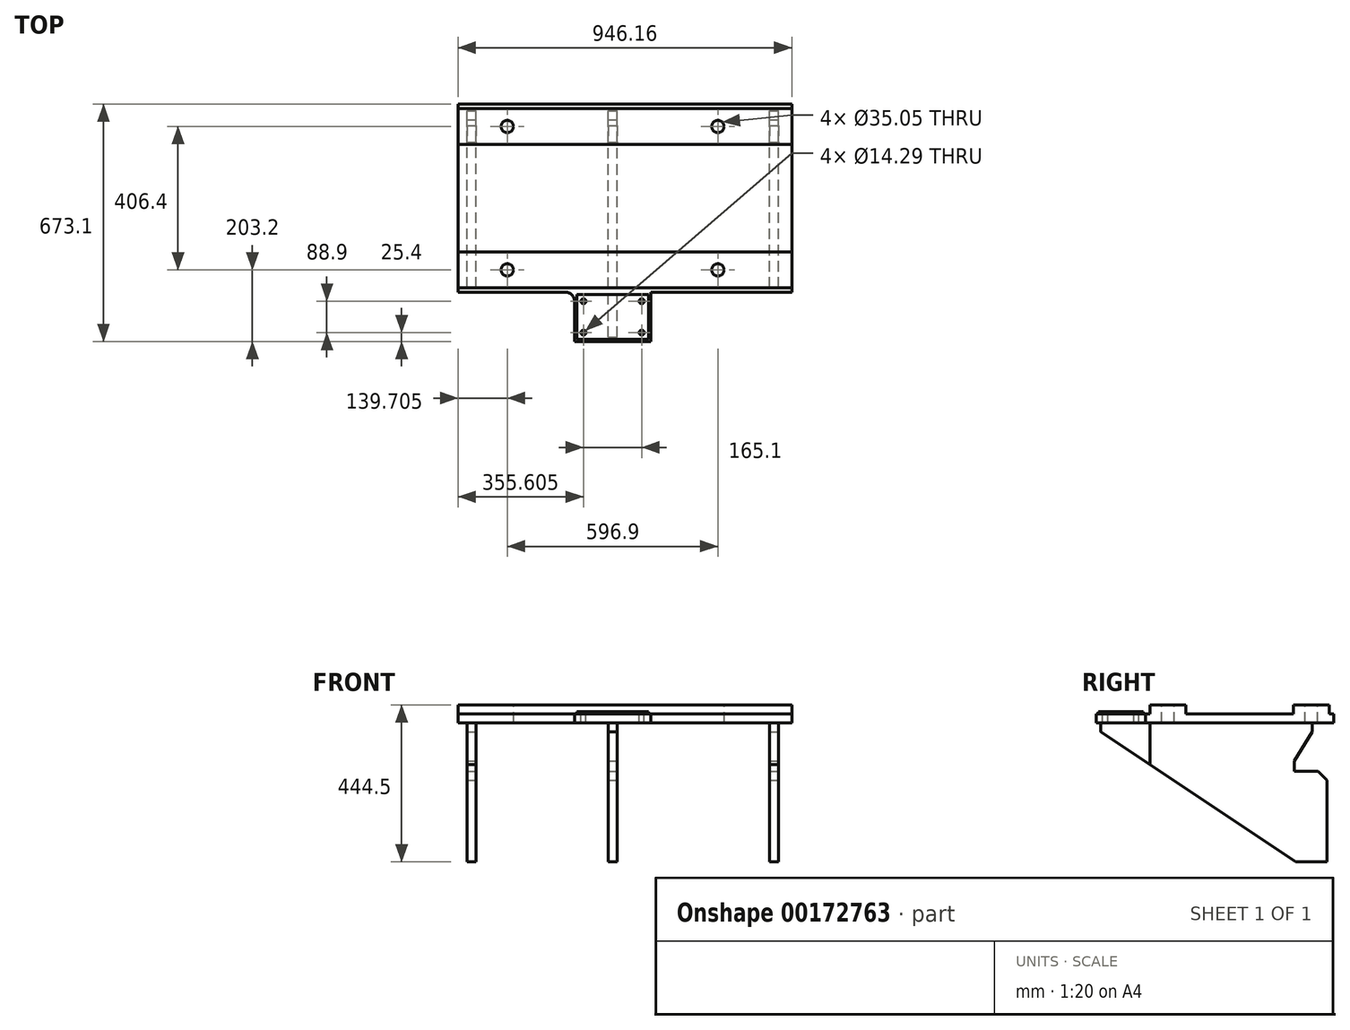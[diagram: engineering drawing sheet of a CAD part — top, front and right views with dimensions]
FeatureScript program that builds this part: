
annotation { "Feature Type Name" : "Feature", "Feature Type Description" : "" }
export const myFeature = defineFeature(function(context is Context, id is Id, definition is map)
    precondition{}
    {
        {
            var Q0;
            Q0=qCreatedBy(makeId("Top.planeOp"),FACE);
            var sketch = newSketch(context, id + "F0", { "sketchPlane" : qUnion([Q0])});
            skLineSegment(sketch, "E0.rect.bottom", {"start": v(-473.07, 266.7) * mm, "end": v(473.08, 266.7) * mm});
            skLineSegment(sketch, "E0.rect.top", {"start": v(-473.08, -266.7) * mm, "end": v(473.07, -266.7) * mm});
            skLineSegment(sketch, "E0.rect.left", {"start": v(-473.08, 266.7) * mm, "end": v(-473.08, -266.7) * mm});
            skLineSegment(sketch, "E0.rect.right", {"start": v(473.08, 266.7) * mm, "end": v(473.07, -266.7) * mm});
            skPoint(sketch, "E0.rect.middle", {"position": v(0, 0) * mm});
            skSolve(sketch);
        }
        {
            var Q0;
            Q0=qSketchRegion(id+"F0",true);
            extrude(context, id + "F1", {"entities" : qUnion([Q0]), "oppositeDirection" : true, "depth" : 25.4 * mm});
        }
        {
            var Q0;
            Q0=makeQuery(id+"F1.opExtrude","CAP_FACE",FACE,{"disambiguationData":[OSD([sQuery(id+"F0.wireOp",EDGE,"E0.rect.bottom"),sQuery(id+"F0.wireOp",EDGE,"E0.rect.top"),sQuery(id+"F0.wireOp",EDGE,"E0.rect.left"),sQuery(id+"F0.wireOp",EDGE,"E0.rect.right")])],"isStart":true});
            var sketch = newSketch(context, id + "F2", { "sketchPlane" : qUnion([Q0])});
            skLineSegment(sketch, "E1.0", {"start": v(-333.38, 266.7) * mm, "end": v(-333.38, -266.7) * mm, "construction": true});
            skLineSegment(sketch, "E2.0", {"start": v(-34.92, 266.7) * mm, "end": v(-34.93, -266.7) * mm, "construction": true});
            skLineSegment(sketch, "E3.0", {"start": v(-473.08, -266.7) * mm, "end": v(473.07, -266.7) * mm});
            skLineSegment(sketch, "E4.0", {"start": v(-473.08, -406.4) * mm, "end": v(473.07, -406.4) * mm});
            skLineSegment(sketch, "E5.0", {"start": v(-142.87, 266.7) * mm, "end": v(-142.88, -266.7) * mm, "construction": true});
            skLineSegment(sketch, "E6.bottom", {"start": v(-142.88, -266.7) * mm, "end": v(73.02, -266.7) * mm});
            skLineSegment(sketch, "E6.top", {"start": v(-142.88, -406.4) * mm, "end": v(73.02, -406.4) * mm});
            skLineSegment(sketch, "E6.left", {"start": v(-142.88, -266.7) * mm, "end": v(-142.88, -406.4) * mm});
            skLineSegment(sketch, "E6.right", {"start": v(73.02, -266.7) * mm, "end": v(73.02, -406.4) * mm});
            skSolve(sketch);
        }
        {
            var Q0;
            Q0=qSketchRegion(id+"F2",true);
            extrude(context, id + "F3", {"entities" : qUnion([Q0]), "operationType" : NewBodyOperationType.ADD, "oppositeDirection" : true, "depth" : 25.4 * mm});
        }
        {
            var Q0;
            Q0=makeQuery(id+"F3.opExtrude","SWEPT_EDGE",EDGE,{"disambiguationData":[OSD([sQuery(id+"F2.wireOp",EDGE,"E3.0"),sQuery(id+"F2.wireOp",EDGE,"E6.bottom"),sQuery(id+"F2.wireOp",EDGE,"E6.left")])]});
            var Q1;
            Q1=makeQuery(id+"F3.opExtrude","SWEPT_EDGE",EDGE,{"disambiguationData":[OSD([sQuery(id+"F2.wireOp",EDGE,"E3.0"),sQuery(id+"F2.wireOp",EDGE,"E6.bottom"),sQuery(id+"F2.wireOp",EDGE,"E6.right")])]});
            fillet(context, id + "F4", {"entities" : qUnion([Q0, Q1]), "radius" : 25.4 * mm, "tangentPropagation" : true, "allowEdgeOverflow" : false});
        }
        {
            var Q0;
            Q0=makeQuery(id+"F3.boolean.opBoolean","MERGE",FACE,{"derivedFrom":[makeQuery(id+"F1.opExtrude","CAP_FACE",FACE,{"disambiguationData":[OSD([sQuery(id+"F0.wireOp",EDGE,"E0.rect.bottom"),sQuery(id+"F0.wireOp",EDGE,"E0.rect.top"),sQuery(id+"F0.wireOp",EDGE,"E0.rect.left"),sQuery(id+"F0.wireOp",EDGE,"E0.rect.right")])],"isStart":true}),makeQuery(id+"F3.opExtrude","CAP_FACE",FACE,{"disambiguationData":[OSD([sQuery(id+"F2.wireOp",EDGE,"E6.bottom"),sQuery(id+"F2.wireOp",EDGE,"E6.top"),sQuery(id+"F2.wireOp",EDGE,"E6.left"),sQuery(id+"F2.wireOp",EDGE,"E6.right")])],"isStart":true})]});
            var sketch = newSketch(context, id + "F5", { "sketchPlane" : qUnion([Q0])});
            skLineSegment(sketch, "E7.0", {"start": v(-473.08, 254) * mm, "end": v(473.08, 254) * mm});
            skLineSegment(sketch, "E8.0", {"start": v(-473.08, 152.4) * mm, "end": v(473.08, 152.4) * mm});
            skLineSegment(sketch, "E9.0", {"start": v(-473.08, -152.4) * mm, "end": v(473.08, -152.4) * mm});
            skLineSegment(sketch, "E10.0", {"start": v(-473.08, -254) * mm, "end": v(473.08, -254) * mm});
            skLineSegment(sketch, "E11.0", {"start": v(473.08, 266.7) * mm, "end": v(473.07, -266.7) * mm});
            skLineSegment(sketch, "E12.0", {"start": v(-473.08, 266.7) * mm, "end": v(-473.08, -266.7) * mm});
            skSolve(sketch);
        }
        {
            var Q0;
            {var subQ2=sQuery(id+"F5.wireOp",EDGE,"E7.0");Q0=makeQuery(id+"F5.imprint","IMPRINT",FACE,{"disambiguationData":[TD([[makeQuery(id+"F5.imprint","IMPRINT",EDGE,{"derivedFrom":subQ2}),-1.0]])]});}
            var Q1;
            {var subQ2=sQuery(id+"F5.wireOp",EDGE,"E9.0");Q1=makeQuery(id+"F5.imprint","IMPRINT",FACE,{"disambiguationData":[TD([[makeQuery(id+"F5.imprint","IMPRINT",EDGE,{"derivedFrom":subQ2}),-1.0]])]});}
            extrude(context, id + "F6", {"entities" : qUnion([Q0, Q1]), "operationType" : NewBodyOperationType.ADD, "depth" : 25.4 * mm});
        }
        {
            var Q0;
            Q0=makeQuery(id+"F6.opExtrude","CAP_FACE",FACE,{"disambiguationData":[OSD([sQuery(id+"F5.wireOp",EDGE,"E7.0"),sQuery(id+"F5.wireOp",EDGE,"E8.0"),sQuery(id+"F5.wireOp",EDGE,"E11.0"),sQuery(id+"F5.wireOp",EDGE,"E12.0")])],"isStart":false});
            var sketch = newSketch(context, id + "F7", { "sketchPlane" : qUnion([Q0])});
            skLineSegment(sketch, "E13.0", {"start": v(-473.08, 266.7) * mm, "end": v(473.08, 266.7) * mm, "construction": true});
            skLineSegment(sketch, "E14.0", {"start": v(-473.08, 0) * mm, "end": v(473.08, 0) * mm, "construction": true});
            skLineSegment(sketch, "E15.0", {"start": v(-142.88, -406.4) * mm, "end": v(73.02, -406.4) * mm, "construction": true});
            skLineSegment(sketch, "E16", {"start": v(-34.93, -406.4) * mm, "end": v(-34.93, 332.02) * mm, "construction": true});
            skLineSegment(sketch, "E17.0", {"start": v(-473.08, 203.2) * mm, "end": v(473.08, 203.2) * mm, "construction": true});
            skLineSegment(sketch, "E18.0", {"start": v(-473.08, -203.2) * mm, "end": v(473.08, -203.2) * mm, "construction": true});
            skLineSegment(sketch, "E19.0", {"start": v(-333.38, -406.4) * mm, "end": v(-333.38, 332.02) * mm, "construction": true});
            skCircle(sketch, "E20", {"center": v(-333.38, 203.2) * mm, "radius": 17.53 * mm});
            skCircle(sketch, "E21", {"center": v(-333.38, -203.2) * mm, "radius": 17.53 * mm});
            skCircle(sketch, "E22.MirrorC", {"center": v(263.53, -203.2) * mm, "radius": 17.53 * mm});
            skCircle(sketch, "E23.MirrorC", {"center": v(263.53, 203.2) * mm, "radius": 17.53 * mm});
            skSolve(sketch);
        }
        {
            var Q0;
            Q0=qSketchRegion(id+"F7",true);
            extrude(context, id + "F8", {"entities" : qUnion([Q0]), "operationType" : NewBodyOperationType.REMOVE, "endBound" : BoundingType.THROUGH_ALL, "oppositeDirection" : true, "depth" : 25.4 * mm});
        }
        {
            var Q0;
            {var subQ0=sQuery(id+"F0.wireOp",EDGE,"E0.rect.top");var subQ1=sQuery(id+"F0.wireOp",EDGE,"E0.rect.left");var subQ2=sQuery(id+"F0.wireOp",EDGE,"E0.rect.right");var subQ3=sQuery(id+"F2.wireOp",EDGE,"E6.bottom");var subQ4=sQuery(id+"F2.wireOp",EDGE,"E6.top");var subQ5=sQuery(id+"F2.wireOp",EDGE,"E6.left");var subQ6=sQuery(id+"F2.wireOp",EDGE,"E6.right");Q0=makeQuery(id+"F6.boolean.opBoolean","SPLIT",FACE,{"disambiguationData":[TD([makeQuery(id+"F1.opExtrude","SWEPT_FACE",FACE,{"disambiguationData":[OSD([subQ0])]})])],"derivedFrom":makeQuery(id+"F3.boolean.opBoolean","MERGE",FACE,{"derivedFrom":[makeQuery(id+"F1.opExtrude","CAP_FACE",FACE,{"disambiguationData":[OSD([sQuery(id+"F0.wireOp",EDGE,"E0.rect.bottom"),subQ0,subQ1,subQ2])],"isStart":true}),makeQuery(id+"F3.opExtrude","CAP_FACE",FACE,{"disambiguationData":[OSD([subQ3,subQ4,subQ5,subQ6])],"isStart":true})]})});}
            var sketch = newSketch(context, id + "F9", { "sketchPlane" : qUnion([Q0])});
            skLineSegment(sketch, "E24", {"start": v(-34.93, -406.4) * mm, "end": v(-34.93, -216.21) * mm, "construction": true});
            skLineSegment(sketch, "E25.0", {"start": v(-142.88, -400.05) * mm, "end": v(73.02, -400.05) * mm});
            skLineSegment(sketch, "E26.0", {"start": v(-142.88, -273.05) * mm, "end": v(73.02, -273.05) * mm});
            skLineSegment(sketch, "E27.0", {"start": v(-136.53, -406.4) * mm, "end": v(-136.53, -216.21) * mm});
            skLineSegment(sketch, "E28.0", {"start": v(66.67, -406.4) * mm, "end": v(66.67, -216.21) * mm});
            skSolve(sketch);
        }
        {
            var Q0;
            Q0=qSketchRegion(id+"F9",true);
            extrude(context, id + "F10", {"entities" : qUnion([Q0]), "operationType" : NewBodyOperationType.ADD, "depth" : 6.35 * mm});
        }
        {
            var Q0;
            Q0=makeQuery(id+"F10.opExtrude","CAP_FACE",FACE,{"disambiguationData":[OSD([sQuery(id+"F9.wireOp",EDGE,"E25.0"),sQuery(id+"F9.wireOp",EDGE,"E26.0"),sQuery(id+"F9.wireOp",EDGE,"E27.0"),sQuery(id+"F9.wireOp",EDGE,"E28.0")])],"isStart":false});
            var sketch = newSketch(context, id + "F11", { "sketchPlane" : qUnion([Q0])});
            skLineSegment(sketch, "E29", {"start": v(-34.93, -400.05) * mm, "end": v(-34.93, -273.05) * mm, "construction": true});
            skLineSegment(sketch, "E30.0", {"start": v(-473.08, 152.4) * mm, "end": v(473.08, 152.4) * mm, "construction": true});
            skLineSegment(sketch, "E31.0", {"start": v(-473.08, -152.4) * mm, "end": v(473.08, -152.4) * mm, "construction": true});
            skLineSegment(sketch, "E32", {"start": v(0, 152.4) * mm, "end": v(0, -152.4) * mm, "construction": true});
            skLineSegment(sketch, "E33", {"start": v(0, 0) * mm, "end": v(-542.05, 0) * mm, "construction": true});
            skLineSegment(sketch, "E34.0", {"start": v(0, -203.2) * mm, "end": v(-542.05, -203.2) * mm, "construction": true});
            skLineSegment(sketch, "E35.0", {"start": v(0, -292.1) * mm, "end": v(-542.05, -292.1) * mm, "construction": true});
            skLineSegment(sketch, "E36.0", {"start": v(0, -381) * mm, "end": v(-542.05, -381) * mm, "construction": true});
            skLineSegment(sketch, "E37.0", {"start": v(-117.48, -400.05) * mm, "end": v(-117.48, -273.05) * mm, "construction": true});
            skPoint(sketch, "E38", {"position": v(-117.48, -292.1) * mm});
            skPoint(sketch, "E39", {"position": v(-117.48, -381) * mm});
            skPoint(sketch, "E40.MirrorP", {"position": v(47.62, -381) * mm});
            skPoint(sketch, "E41.MirrorP", {"position": v(47.62, -292.1) * mm});
            skSolve(sketch);
        }
        {
            var Q0;
            Q0=sQuery(id+"F11.wireOp",VERTEX,"E38");
            var Q1;
            Q1=sQuery(id+"F11.wireOp",VERTEX,"E39");
            var Q2;
            Q2=sQuery(id+"F11.wireOp",VERTEX,"E41.MirrorP");
            var Q3;
            Q3=sQuery(id+"F11.wireOp",VERTEX,"E40.MirrorP");
            var Q4;
            Q4=makeQuery(id+"F1.opExtrude","SWEPT_BODY",BODY,{"disambiguationData":[OSD([sQuery(id+"F0.wireOp",EDGE,"E0.rect.bottom"),sQuery(id+"F0.wireOp",EDGE,"E0.rect.top"),sQuery(id+"F0.wireOp",EDGE,"E0.rect.left"),sQuery(id+"F0.wireOp",EDGE,"E0.rect.right")])]});
            hole(context, id + "F12", {"style" : HoleStyle.SIMPLE, "holeDiameter" : 14.29 * mm, "endStyle" : HoleEndStyle.THROUGH, "locations" : qUnion([Q0, Q1, Q2, Q3]), "scope" : qUnion([Q4])});
        }
        {
            var Q0;
            Q0=makeQuery(id+"F3.boolean.opBoolean","MERGE",FACE,{"derivedFrom":[makeQuery(id+"F1.opExtrude","CAP_FACE",FACE,{"disambiguationData":[OSD([sQuery(id+"F0.wireOp",EDGE,"E0.rect.bottom"),sQuery(id+"F0.wireOp",EDGE,"E0.rect.top"),sQuery(id+"F0.wireOp",EDGE,"E0.rect.left"),sQuery(id+"F0.wireOp",EDGE,"E0.rect.right")])],"isStart":false}),makeQuery(id+"F3.opExtrude","CAP_FACE",FACE,{"disambiguationData":[OSD([sQuery(id+"F2.wireOp",EDGE,"E6.bottom"),sQuery(id+"F2.wireOp",EDGE,"E6.top"),sQuery(id+"F2.wireOp",EDGE,"E6.left"),sQuery(id+"F2.wireOp",EDGE,"E6.right")])],"isStart":false})]});
            var sketch = newSketch(context, id + "F13", { "sketchPlane" : qUnion([Q0])});
            skLineSegment(sketch, "E42.0", {"start": v(-473.08, -247.65) * mm, "end": v(473.08, -247.65) * mm});
            skLineSegment(sketch, "E43", {"start": v(-34.93, 406.4) * mm, "end": v(-34.93, -266.7) * mm, "construction": true});
            skLineSegment(sketch, "E44.0", {"start": v(-473.08, 393.45) * mm, "end": v(473.08, 393.45) * mm});
            skLineSegment(sketch, "E45.0", {"start": v(-473.08, 254) * mm, "end": v(-422.28, 254) * mm});
            skLineSegment(sketch, "E46.0", {"start": v(-47.63, 393.45) * mm, "end": v(-47.63, -247.65) * mm});
            skLineSegment(sketch, "E47.0", {"start": v(-22.23, 393.45) * mm, "end": v(-22.23, -247.65) * mm});
            skLineSegment(sketch, "E48.0", {"start": v(-447.68, 406.4) * mm, "end": v(-447.68, 393.45) * mm});
            skLineSegment(sketch, "E49.0", {"start": v(-422.28, 406.4) * mm, "end": v(-422.28, 393.45) * mm});
            skLineSegment(sketch, "E50.0", {"start": v(434.98, 406.4) * mm, "end": v(434.98, 393.45) * mm});
            skLineSegment(sketch, "E51.0", {"start": v(409.58, 406.4) * mm, "end": v(409.58, 393.45) * mm});
            skLineSegment(sketch, "E52.trimOffspring", {"start": v(-447.68, 254) * mm, "end": v(-447.68, -247.65) * mm});
            skLineSegment(sketch, "E53.trimOffspring", {"start": v(-422.28, 254) * mm, "end": v(-422.28, -247.65) * mm});
            skLineSegment(sketch, "E54.trimOffspring", {"start": v(409.58, 254) * mm, "end": v(409.58, -247.65) * mm});
            skLineSegment(sketch, "E55.trimOffspring", {"start": v(434.98, 254) * mm, "end": v(434.98, -247.65) * mm});
            skLineSegment(sketch, "E56.trimOffspring", {"start": v(409.58, 254) * mm, "end": v(473.08, 254) * mm});
            skLineSegment(sketch, "E57.trimOffspring", {"start": v(-47.63, 254) * mm, "end": v(-22.23, 254) * mm, "construction": true});
            skSolve(sketch);
        }
        {
            var Q0;
            {var subQ2=sQuery(id+"F13.wireOp",EDGE,"E54.trimOffspring");Q0=makeQuery(id+"F13.imprint","IMPRINT",FACE,{"disambiguationData":[TD([[makeQuery(id+"F13.imprint","IMPRINT",EDGE,{"derivedFrom":subQ2}),1.0]])]});}
            var Q1;
            {var subQ1=sQuery(id+"F13.wireOp",EDGE,"E46.0");Q1=makeQuery(id+"F13.imprint","IMPRINT",FACE,{"disambiguationData":[TD([[makeQuery(id+"F13.imprint","IMPRINT",EDGE,{"derivedFrom":subQ1}),1.0]])]});}
            var Q2;
            {var subQ1=sQuery(id+"F13.wireOp",EDGE,"E52.trimOffspring");Q2=makeQuery(id+"F13.imprint","IMPRINT",FACE,{"disambiguationData":[TD([[makeQuery(id+"F13.imprint","IMPRINT",EDGE,{"derivedFrom":subQ1}),1.0]])]});}
            extrude(context, id + "F14", {"entities" : qUnion([Q0, Q1, Q2]), "operationType" : NewBodyOperationType.ADD, "depth" : 393.7 * mm});
        }
        {
            var Q0;
            Q0=makeQuery(id+"F14.opExtrude","SWEPT_FACE",FACE,{"disambiguationData":[OSD([sQuery(id+"F13.wireOp",EDGE,"E55.trimOffspring")])]});
            var sketch = newSketch(context, id + "F15", { "sketchPlane" : qUnion([Q0])});
            skLineSegment(sketch, "E58.0", {"start": v(-292.1, -25.4) * mm, "end": v(-406.4, -25.4) * mm, "construction": true});
            skLineSegment(sketch, "E59.0", {"start": v(266.7, -25.4) * mm, "end": v(-266.7, -25.4) * mm, "construction": true});
            skLineSegment(sketch, "E60.0", {"start": v(247.65, -419.1) * mm, "end": v(247.65, -25.4) * mm, "construction": true});
            skLineSegment(sketch, "E61.0", {"start": v(-393.45, -419.1) * mm, "end": v(-393.45, -25.4) * mm, "construction": true});
            skLineSegment(sketch, "E62.0", {"start": v(-292.1, -50.8) * mm, "end": v(-406.4, -50.8) * mm, "construction": true});
            skLineSegment(sketch, "E63.0", {"start": v(158.75, -419.1) * mm, "end": v(158.75, -25.4) * mm, "construction": true});
            skLineSegment(sketch, "E64", {"start": v(-393.45, -50.8) * mm, "end": v(158.75, -419.1) * mm});
            skLineSegment(sketch, "E65", {"start": v(-393.45, -50.8) * mm, "end": v(-393.45, -419.1) * mm});
            skLineSegment(sketch, "E66", {"start": v(-393.45, -419.1) * mm, "end": v(158.75, -419.1) * mm});
            skSolve(sketch);
        }
        {
            var Q0;
            Q0=qSketchRegion(id+"F15",true);
            extrude(context, id + "F16", {"entities" : qUnion([Q0]), "operationType" : NewBodyOperationType.REMOVE, "endBound" : BoundingType.THROUGH_ALL, "oppositeDirection" : true, "depth" : 25.4 * mm});
        }
        {
            var Q0;
            Q0=makeQuery(id+"F14.opExtrude","SWEPT_FACE",FACE,{"disambiguationData":[OSD([sQuery(id+"F13.wireOp",EDGE,"E55.trimOffspring")])]});
            var sketch = newSketch(context, id + "F17", { "sketchPlane" : qUnion([Q0])});
            skLineSegment(sketch, "E67.0", {"start": v(155.58, -161.92) * mm, "end": v(222.25, -161.92) * mm});
            skLineSegment(sketch, "E68.0", {"start": v(155.58, -161.92) * mm, "end": v(155.58, -133.35) * mm});
            skLineSegment(sketch, "E69", {"start": v(222.25, -161.92) * mm, "end": v(247.65, -187.32) * mm});
            skLineSegment(sketch, "E70.0", {"start": v(266.7, -25.4) * mm, "end": v(-266.7, -25.4) * mm});
            skLineSegment(sketch, "E71", {"start": v(206.38, -50.8) * mm, "end": v(155.58, -133.35) * mm});
            skLineSegment(sketch, "E72.trimOffspring", {"start": v(206.38, -50.8) * mm, "end": v(206.38, -25.4) * mm});
            skLineSegment(sketch, "E73", {"start": v(206.38, -25.4) * mm, "end": v(247.65, -25.4) * mm});
            skLineSegment(sketch, "E74", {"start": v(247.65, -25.4) * mm, "end": v(247.65, -187.32) * mm});
            skSolve(sketch);
        }
        {
            var Q0;
            Q0=qSketchRegion(id+"F17",true);
            extrude(context, id + "F18", {"entities" : qUnion([Q0]), "operationType" : NewBodyOperationType.REMOVE, "endBound" : BoundingType.THROUGH_ALL, "oppositeDirection" : true, "depth" : 25.4 * mm});
        }
    });
